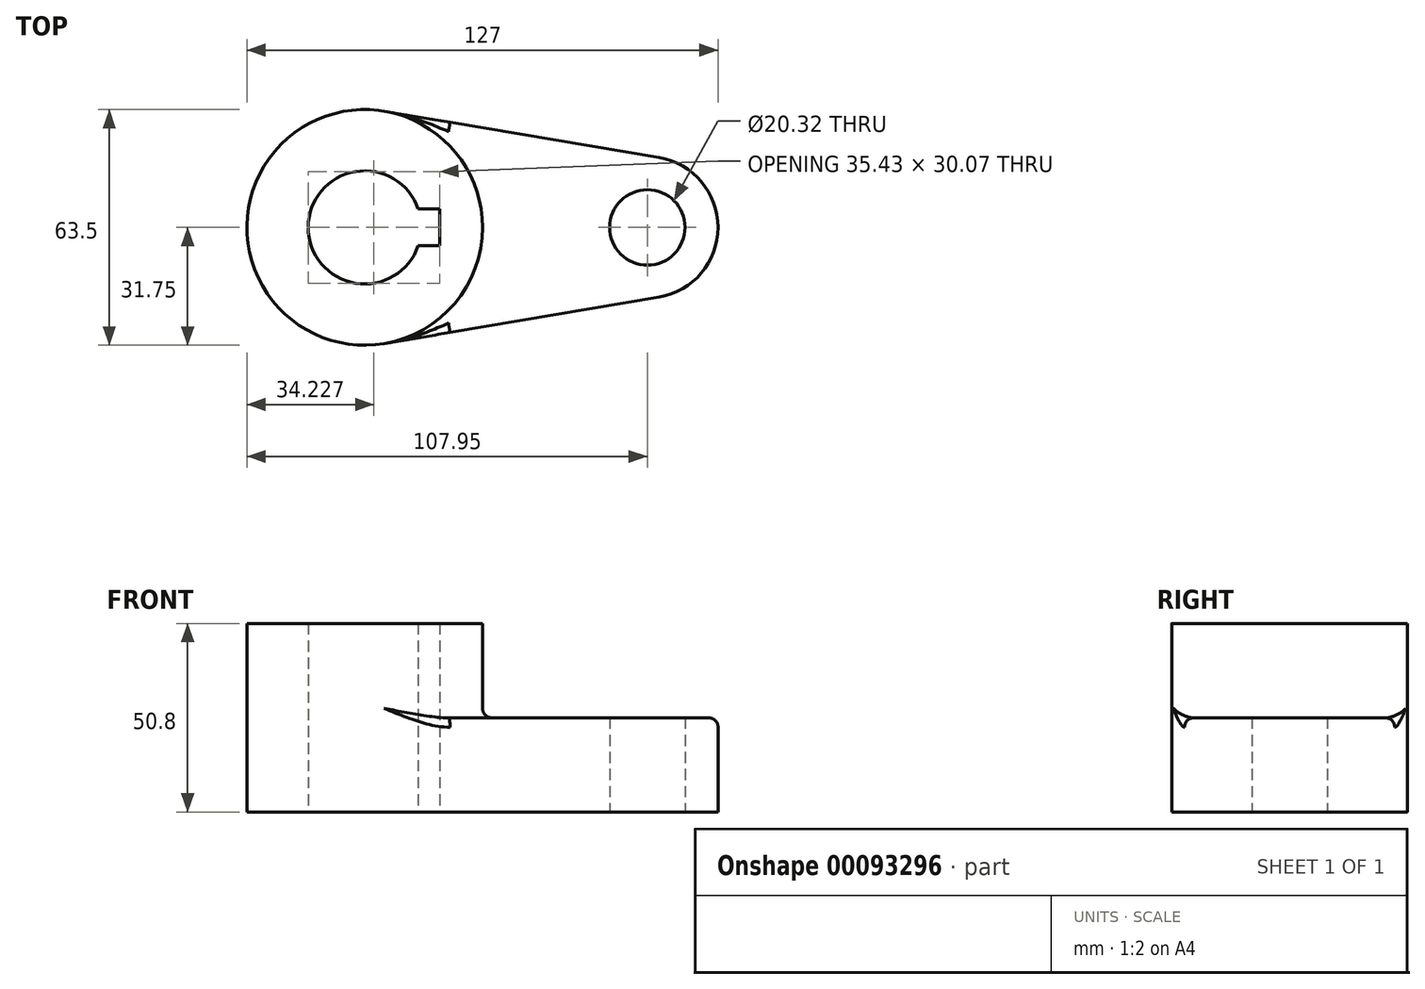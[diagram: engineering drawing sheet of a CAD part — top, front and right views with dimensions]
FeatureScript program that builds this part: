
annotation { "Feature Type Name" : "Feature", "Feature Type Description" : "" }
export const myFeature = defineFeature(function(context is Context, id is Id, definition is map)
    precondition{}
    {
        {
            var Q0;
            Q0=qCreatedBy(makeId("Top.planeOp"),FACE);
            var sketch = newSketch(context, id + "F0", { "sketchPlane" : qUnion([Q0])});
            skCircle(sketch, "E0", {"center": v(0, 0) * mm, "radius": 31.75 * mm});
            skCircle(sketch, "E1", {"center": v(76.2, 0) * mm, "radius": 19.05 * mm});
            skLineSegment(sketch, "E2", {"start": v(5.3, 31.3) * mm, "end": v(79.38, 18.78) * mm});
            skLineSegment(sketch, "E3", {"start": v(5.3, -31.3) * mm, "end": v(79.38, -18.78) * mm});
            skCircle(sketch, "E4", {"center": v(0, 0) * mm, "radius": 15.24 * mm});
            skCircle(sketch, "E5", {"center": v(76.2, 0) * mm, "radius": 10.16 * mm});
            skLineSegment(sketch, "E6.bottom", {"start": v(20.2, -4.94) * mm, "end": v(-20.2, -4.94) * mm});
            skLineSegment(sketch, "E6.top", {"start": v(20.2, 4.94) * mm, "end": v(-20.2, 4.94) * mm});
            skLineSegment(sketch, "E6.left", {"start": v(20.2, -4.94) * mm, "end": v(20.2, 4.94) * mm});
            skLineSegment(sketch, "E6.right", {"start": v(-20.2, -4.94) * mm, "end": v(-20.2, 4.94) * mm});
            skSolve(sketch);
        }
        {
            var Q0;
            {var subQ11=sQuery(id+"F0.wireOp",EDGE,"E6.left");Q0=makeQuery(id+"F0.imprint","IMPRINT",FACE,{"disambiguationData":[TD([[makeQuery(id+"F0.imprint","IMPRINT",EDGE,{"derivedFrom":subQ11}),-1.0]])]});}
            var Q1;
            {var subQ5=sQuery(id+"F0.wireOp",EDGE,"E6.right");Q1=makeQuery(id+"F0.imprint","IMPRINT",FACE,{"disambiguationData":[TD([[makeQuery(id+"F0.imprint","IMPRINT",EDGE,{"derivedFrom":subQ5}),-1.0]])]});}
            var Q2;
            {var subQ0=sQuery(id+"F0.wireOp",EDGE,"E2");Q2=makeQuery(id+"F0.imprint","IMPRINT",FACE,{"disambiguationData":[TD([[makeQuery(id+"F0.imprint","IMPRINT",EDGE,{"derivedFrom":subQ0}),-1.0]])]});}
            var Q3;
            Q3=makeQuery(id+"F0.imprint","IMPRINT",FACE,{"disambiguationData":[TD([[makeQuery(id+"F0.imprint","IMPRINT",EDGE,{"derivedFrom":sQuery(id+"F0.wireOp",EDGE,"E5")}),-1.0]])]});
            extrude(context, id + "F1", {"entities" : qUnion([Q0, Q1, Q2, Q3]), "depth" : 25.4 * mm});
        }
        {
            var Q0;
            {var subQ11=sQuery(id+"F0.wireOp",EDGE,"E6.left");Q0=makeQuery(id+"F0.imprint","IMPRINT",FACE,{"disambiguationData":[TD([[makeQuery(id+"F0.imprint","IMPRINT",EDGE,{"derivedFrom":subQ11}),-1.0]])]});}
            var Q1;
            {var subQ5=sQuery(id+"F0.wireOp",EDGE,"E6.right");Q1=makeQuery(id+"F0.imprint","IMPRINT",FACE,{"disambiguationData":[TD([[makeQuery(id+"F0.imprint","IMPRINT",EDGE,{"derivedFrom":subQ5}),-1.0]])]});}
            extrude(context, id + "F2", {"entities" : qUnion([Q0, Q1]), "operationType" : NewBodyOperationType.ADD, "depth" : 50.8 * mm});
        }
        {
            var Q0;
            {var subQ0=sQuery(id+"F0.wireOp",EDGE,"E0");Q0=makeQuery(id+"F2.boolean.opBoolean","INTERSECT",EDGE,{"derivedFrom":[makeQuery(id+"F1.opExtrude","CAP_FACE",FACE,{"disambiguationData":[OSD([subQ0,sQuery(id+"F0.wireOp",EDGE,"E1"),sQuery(id+"F0.wireOp",EDGE,"E2"),sQuery(id+"F0.wireOp",EDGE,"E3"),sQuery(id+"F0.wireOp",EDGE,"E4"),sQuery(id+"F0.wireOp",EDGE,"E5"),sQuery(id+"F0.wireOp",EDGE,"E6.bottom"),sQuery(id+"F0.wireOp",EDGE,"E6.top"),sQuery(id+"F0.wireOp",EDGE,"E6.left")])],"isStart":false}),makeQuery(id+"F2.opExtrude","SWEPT_FACE",FACE,{"disambiguationData":[OSD([subQ0])]})]});}
            fillet(context, id + "F3", {"entities" : qUnion([Q0]), "radius" : 2.54 * mm, "tangentPropagation" : true, "allowEdgeOverflow" : false});
        }
        {
            var Q0;
            Q0=makeQuery(id+"F1.opExtrude","CAP_EDGE",EDGE,{"disambiguationData":[OSD([sQuery(id+"F0.wireOp",EDGE,"E3")])],"isStart":false});
            fillet(context, id + "F4", {"entities" : qUnion([Q0]), "radius" : 2.54 * mm, "tangentPropagation" : true, "allowEdgeOverflow" : false});
        }
    });
